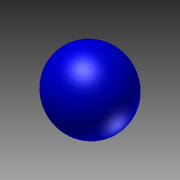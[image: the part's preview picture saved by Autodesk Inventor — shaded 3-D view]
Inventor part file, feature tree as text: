
AUTODESK INVENTOR PART (.ipt)
format: ipt  version: 2012 (Build 160160000, 160)  size: 118,272 bytes
history: native  units: in
note: dims shown in document units (in); Inventor stores cm internally (conversion verified against a paired STEP export)
features: extrude x1, fillet x1, sketch x1
ambient origin geometry x8: Origin, YZ Plane, XZ Plane, XY Plane, X Axis, Y Axis, Z Axis, Center Point
bodies: Solid1 (feature_tree)
feature tree (3):
  extrude  "Extrusion1"  Depth=5.8in TaperAngle=0.0deg
  fillet  "Fillet1"  Radius=2.9in
  sketch  "Sketch1"  dims[d0=6.3in d1=5.8in d2=0.0in d3=2.9in]
